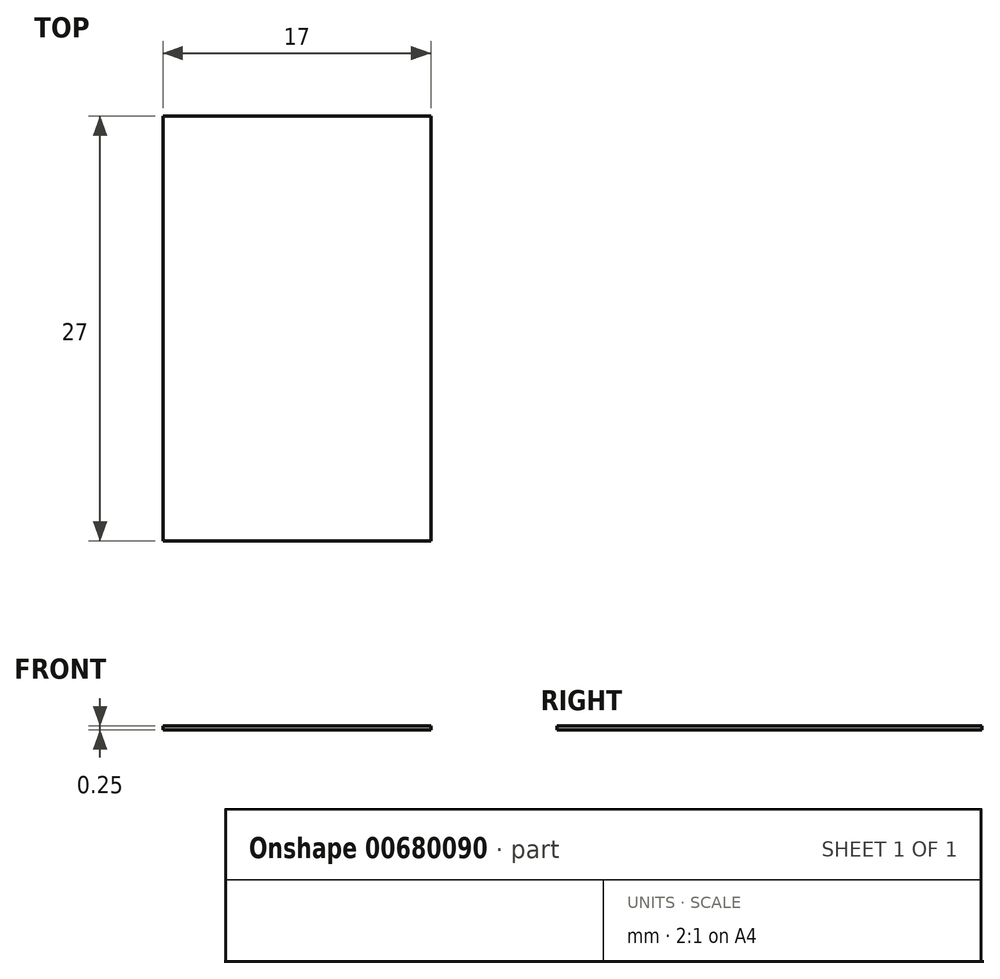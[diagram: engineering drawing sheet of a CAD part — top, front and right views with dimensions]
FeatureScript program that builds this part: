
annotation { "Feature Type Name" : "Feature", "Feature Type Description" : "" }
export const myFeature = defineFeature(function(context is Context, id is Id, definition is map)
    precondition{}
    {
        {
            var Q0;
            Q0=qCreatedBy(makeId("Top.planeOp"),FACE);
            var sketch = newSketch(context, id + "F0", { "sketchPlane" : qUnion([Q0])});
            skLineSegment(sketch, "E0.bottom", {"start": v(8.5, -13.5) * mm, "end": v(-8.5, -13.5) * mm});
            skLineSegment(sketch, "E0.top", {"start": v(8.5, 13.5) * mm, "end": v(-8.5, 13.5) * mm});
            skLineSegment(sketch, "E0.left", {"start": v(8.5, -13.5) * mm, "end": v(8.5, 13.5) * mm});
            skLineSegment(sketch, "E0.right", {"start": v(-8.5, -13.5) * mm, "end": v(-8.5, 13.5) * mm});
            skPoint(sketch, "E0.middle", {"position": v(0, 0) * mm});
            skSolve(sketch);
        }
        {
            var Q0;
            Q0=makeQuery(id+"F0.imprint","IMPRINT",FACE,{"disambiguationData":[TD([[makeQuery(id+"F0.imprint","IMPRINT",EDGE,{"derivedFrom":sQuery(id+"F0.wireOp",EDGE,"E0.bottom")}),-1.0]])]});
            extrude(context, id + "F1", {"entities" : qUnion([Q0]), "depth" : 0.25 * mm, "offsetDistance" : 25.4 * mm});
        }
    });
